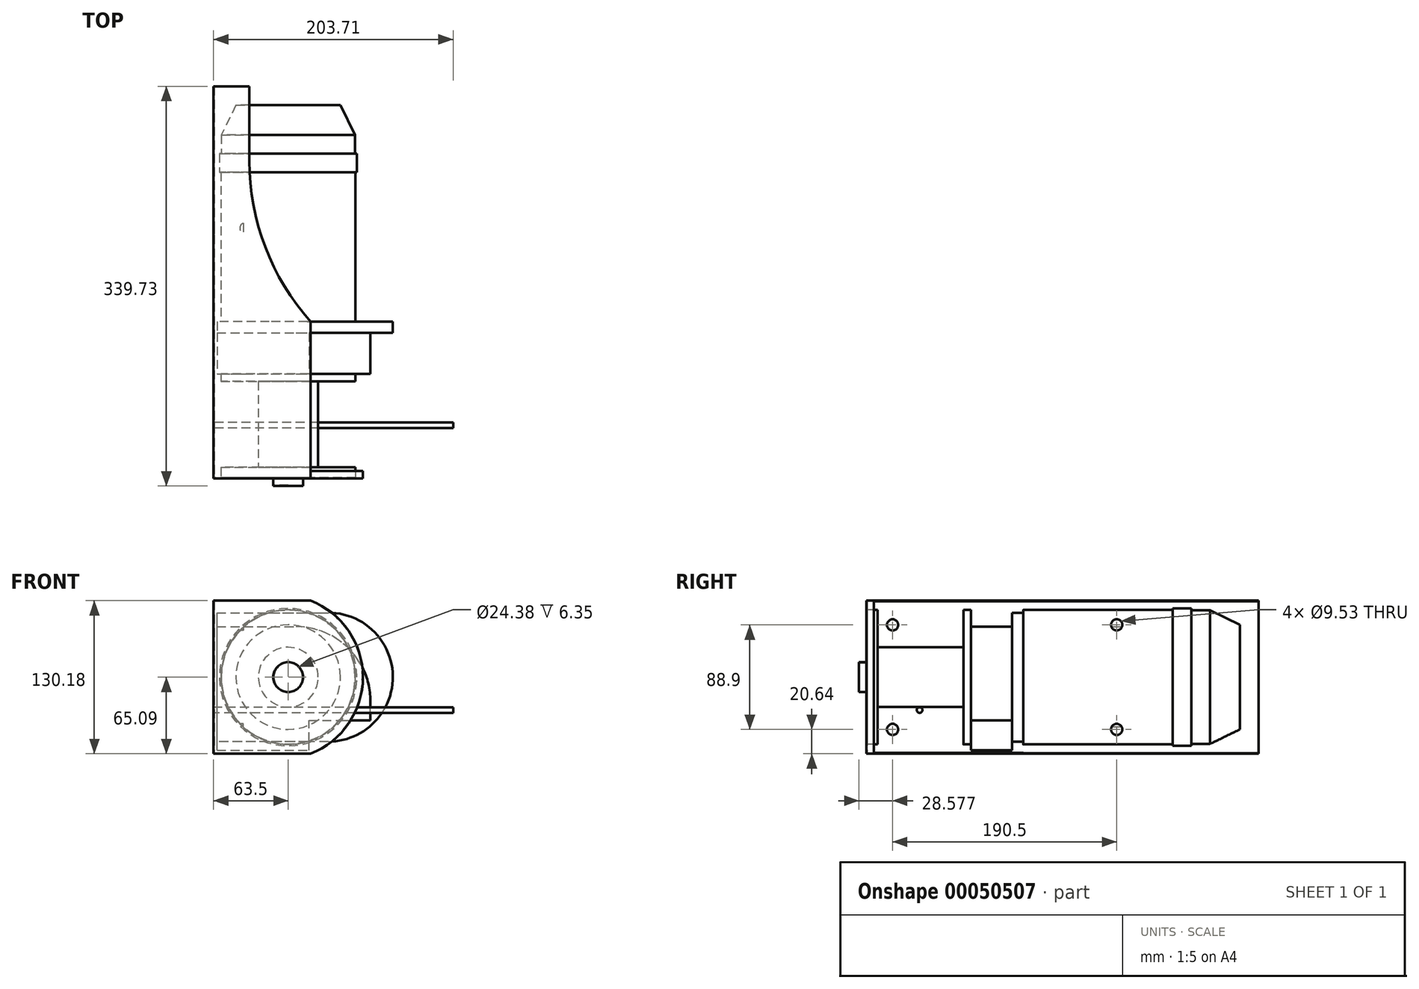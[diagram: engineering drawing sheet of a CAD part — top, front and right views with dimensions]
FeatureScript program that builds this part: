
annotation { "Feature Type Name" : "Feature", "Feature Type Description" : "" }
export const myFeature = defineFeature(function(context is Context, id is Id, definition is map)
    precondition{}
    {
        {
            var Q0;
            Q0=qCreatedBy(makeId("Right.planeOp"),FACE);
            var sketch = newSketch(context, id + "F0", { "sketchPlane" : qUnion([Q0])});
            skLineSegment(sketch, "E0.rect.bottom", {"start": v(166.69, 65.09) * mm, "end": v(-166.69, 65.09) * mm});
            skLineSegment(sketch, "E0.rect.top", {"start": v(166.69, -65.09) * mm, "end": v(-166.69, -65.09) * mm});
            skLineSegment(sketch, "E0.rect.left", {"start": v(166.69, 65.09) * mm, "end": v(166.69, -65.09) * mm});
            skLineSegment(sketch, "E0.rect.right", {"start": v(-166.69, 65.09) * mm, "end": v(-166.69, -65.09) * mm});
            skPoint(sketch, "E0.rect.middle", {"position": v(0, 0) * mm});
            skSolve(sketch);
        }
        {
            var Q0;
            Q0 = qSketchRegion(id + "F0", true);
            extrude(context, id + "F1", {"entities" : qUnion([Q0]), "endBound" : BoundingType.SYMMETRIC, "depth" : 127 * mm});
        }
        {
            var Q0;
            Q0=makeQuery(id+"F1.opExtrude","SWEPT_FACE",FACE,{"disambiguationData":[OSD([sQuery(id+"F0.wireOp",EDGE,"E0.rect.right")])]});
            var sketch = newSketch(context, id + "F2", { "sketchPlane" : qUnion([Q0])});
            skArc(sketch, "E1", {"start": v(19.05, -65.09) * mm, "mid": v(63.5, 0) * mm, "end": v(19.05, 65.09) * mm});
            skLineSegment(sketch, "E2", {"start": v(19.05, 65.09) * mm, "end": v(63.5, 65.09) * mm});
            skLineSegment(sketch, "E3", {"start": v(63.5, 65.09) * mm, "end": v(63.5, -65.09) * mm});
            skLineSegment(sketch, "E4", {"start": v(63.5, -65.09) * mm, "end": v(19.05, -65.09) * mm});
            skSolve(sketch);
        }
        {
            var Q0;
            Q0 = qSketchRegion(id + "F2", true);
            extrude(context, id + "F3", {"entities" : qUnion([Q0]), "operationType" : NewBodyOperationType.REMOVE, "endBound" : BoundingType.UP_TO_NEXT, "oppositeDirection" : true, "depth" : 25.4 * mm});
        }
        {
            var Q0;
            Q0=makeQuery(id+"F1.opExtrude","SWEPT_FACE",FACE,{"disambiguationData":[OSD([sQuery(id+"F0.wireOp",EDGE,"E0.rect.bottom")])]});
            var sketch = newSketch(context, id + "F4", { "sketchPlane" : qUnion([Q0])});
            skLineSegment(sketch, "E5", {"start": v(-33.02, 166.69) * mm, "end": v(-33.02, 103.19) * mm});
            skArc(sketch, "E6", {"start": v(-33.02, 103.19) * mm, "mid": v(-19.56, 30.13) * mm, "end": v(19.05, -33.34) * mm});
            skLineSegment(sketch, "E7", {"start": v(-33.02, 166.69) * mm, "end": v(63.5, 166.69) * mm});
            skLineSegment(sketch, "E8", {"start": v(63.5, 166.69) * mm, "end": v(63.5, -160.34) * mm});
            skLineSegment(sketch, "E9", {"start": v(63.5, -160.34) * mm, "end": v(19.05, -160.34) * mm});
            skLineSegment(sketch, "E10", {"start": v(19.05, -160.34) * mm, "end": v(19.05, -33.34) * mm});
            skSolve(sketch);
        }
        {
            var Q0;
            Q0 = qSketchRegion(id + "F4", true);
            extrude(context, id + "F5", {"entities" : qUnion([Q0]), "operationType" : NewBodyOperationType.REMOVE, "endBound" : BoundingType.UP_TO_NEXT, "oppositeDirection" : true, "depth" : 25.4 * mm});
        }
        {
            var Q0;
            Q0=makeQuery(id+"F1.opExtrude","SWEPT_FACE",FACE,{"disambiguationData":[OSD([sQuery(id+"F0.wireOp",EDGE,"E0.rect.right")])]});
            var sketch = newSketch(context, id + "F6", { "sketchPlane" : qUnion([Q0])});
            skCircle(sketch, "E11", {"center": v(0, 0) * mm, "radius": 12.7 * mm});
            skSolve(sketch);
        }
        {
            var Q0;
            Q0 = qSketchRegion(id + "F6", true);
            extrude(context, id + "F7", {"entities" : qUnion([Q0]), "operationType" : NewBodyOperationType.ADD, "depth" : 6.35 * mm});
        }
        {
            var Q0;
            Q0=makeQuery(id+"F1.opExtrude","SWEPT_FACE",FACE,{"disambiguationData":[OSD([sQuery(id+"F0.wireOp",EDGE,"E0.rect.left")])]});
            var Q1;
            Q1=makeQuery(id+"F5.boolean.opBoolean","COPY",FACE,{"derivedFrom":makeQuery(id+"F5.opExtrude","SWEPT_FACE",FACE,{"disambiguationData":[OSD([sQuery(id+"F4.wireOp",EDGE,"E5")])]})});
            var Q2;
            Q2=makeQuery(id+"F5.boolean.opBoolean","COPY",FACE,{"derivedFrom":makeQuery(id+"F5.opExtrude","SWEPT_FACE",FACE,{"disambiguationData":[OSD([sQuery(id+"F4.wireOp",EDGE,"E6")])]})});
            var Q3;
            Q3=makeQuery(id+"F5.boolean.opBoolean","COPY",FACE,{"derivedFrom":makeQuery(id+"F5.opExtrude","SWEPT_FACE",FACE,{"disambiguationData":[OSD([sQuery(id+"F4.wireOp",EDGE,"E10")])]})});
            var Q4;
            Q4=makeQuery(id+"F5.boolean.opBoolean","COPY",FACE,{"derivedFrom":makeQuery(id+"F5.opExtrude","SWEPT_FACE",FACE,{"disambiguationData":[OSD([sQuery(id+"F4.wireOp",EDGE,"E9")])]})});
            shell(context, id + "F8", {"entities" : qUnion([Q0, Q1, Q2, Q3, Q4]), "thickness" : 0.5 * mm});
        }
        {
            var Q0;
            Q0=makeQuery(id+"F8.opShell","OFFSET_FACE",FACE,{"disambiguationData":[OSD([sQuery(id+"F0.wireOp",EDGE,"E0.rect.right")])]});
            var sketch = newSketch(context, id + "F9", { "sketchPlane" : qUnion([Q0])});
            skCircle(sketch, "E12", {"center": v(0, 0) * mm, "radius": 57.15 * mm});
            skSolve(sketch);
        }
        {
            var Q0;
            Q0 = qSketchRegion(id + "F9", true);
            extrude(context, id + "F10", {"entities" : qUnion([Q0]), "operationType" : NewBodyOperationType.ADD, "depth" : 8.9 * mm});
        }
        {
            var Q0;
            Q0=makeQuery(id+"F10.opExtrude","CAP_FACE",FACE,{"disambiguationData":[OSD([sQuery(id+"F9.wireOp",EDGE,"E12")])],"isStart":false});
            var sketch = newSketch(context, id + "F11", { "sketchPlane" : qUnion([Q0])});
            skCircle(sketch, "E13", {"center": v(0, 0) * mm, "radius": 25.4 * mm});
            skSolve(sketch);
        }
        {
            var Q0;
            Q0 = qSketchRegion(id + "F11", true);
            extrude(context, id + "F12", {"entities" : qUnion([Q0]), "operationType" : NewBodyOperationType.ADD, "depth" : 73.02 * mm});
        }
        {
            var Q0;
            Q0=makeQuery(id+"F12.opExtrude","CAP_FACE",FACE,{"disambiguationData":[OSD([sQuery(id+"F11.wireOp",EDGE,"E13")])],"isStart":false});
            var sketch = newSketch(context, id + "F13", { "sketchPlane" : qUnion([Q0])});
            skCircle(sketch, "E14", {"center": v(0, 0) * mm, "radius": 57.15 * mm});
            skSolve(sketch);
        }
        {
            var Q0;
            Q0 = qSketchRegion(id + "F13", true);
            extrude(context, id + "F14", {"entities" : qUnion([Q0]), "operationType" : NewBodyOperationType.ADD, "depth" : 6.35 * mm});
        }
        {
            var Q0;
            Q0=makeQuery(id+"F14.opExtrude","CAP_FACE",FACE,{"disambiguationData":[OSD([sQuery(id+"F13.wireOp",EDGE,"E14")])],"isStart":false});
            var sketch = newSketch(context, id + "F15", { "sketchPlane" : qUnion([Q0])});
            skLineSegment(sketch, "E15", {"start": v(60.45, -62.04) * mm, "end": v(-17.58, -62.04) * mm});
            skLineSegment(sketch, "E16", {"start": v(-17.58, -62.04) * mm, "end": v(-17.58, -36.64) * mm});
            skLineSegment(sketch, "E17", {"start": v(-17.58, -36.64) * mm, "end": v(-69.85, -36.64) * mm});
            skLineSegment(sketch, "E18", {"start": v(60.45, -62.04) * mm, "end": v(60.45, 42.86) * mm});
            skLineSegment(sketch, "E19", {"start": v(60.45, 42.86) * mm, "end": v(-6.7, 42.86) * mm});
            skLineSegment(sketch, "E20", {"start": v(-69.85, -36.64) * mm, "end": v(-69.85, -20.3) * mm});
            skArc(sketch, "E21", {"start": v(-6.7, 42.86) * mm, "mid": v(-51.35, 24.36) * mm, "end": v(-69.85, -20.3) * mm});
            skSolve(sketch);
        }
        {
            var Q0;
            Q0 = qSketchRegion(id + "F15", true);
            extrude(context, id + "F16", {"entities" : qUnion([Q0]), "operationType" : NewBodyOperationType.ADD, "depth" : 34.92 * mm});
        }
        {
            var Q0;
            Q0=makeQuery(id+"F16.opExtrude","CAP_FACE",FACE,{"disambiguationData":[OSD([sQuery(id+"F15.wireOp",EDGE,"E15"),sQuery(id+"F15.wireOp",EDGE,"E16"),sQuery(id+"F15.wireOp",EDGE,"E17"),sQuery(id+"F15.wireOp",EDGE,"E18"),sQuery(id+"F15.wireOp",EDGE,"E19"),sQuery(id+"F15.wireOp",EDGE,"E20"),sQuery(id+"F15.wireOp",EDGE,"E21")])],"isStart":false});
            var sketch = newSketch(context, id + "F17", { "sketchPlane" : qUnion([Q0])});
            skArc(sketch, "E22", {"start": v(-34.1, 54.8) * mm, "mid": v(-88.9, 0) * mm, "end": v(-34.1, -54.8) * mm});
            skLineSegment(sketch, "E23", {"start": v(-34.1, -54.8) * mm, "end": v(60.45, -54.8) * mm});
            skLineSegment(sketch, "E24", {"start": v(60.45, -54.8) * mm, "end": v(60.45, 54.8) * mm});
            skLineSegment(sketch, "E25", {"start": v(60.45, 54.8) * mm, "end": v(-34.1, 54.8) * mm});
            skLineSegment(sketch, "E26", {"start": v(-34.1, 0) * mm, "end": v(-88.9, 0) * mm, "construction": true});
            skSolve(sketch);
        }
        {
            var Q0;
            Q0 = qSketchRegion(id + "F17", true);
            extrude(context, id + "F18", {"entities" : qUnion([Q0]), "operationType" : NewBodyOperationType.ADD, "depth" : 9.52 * mm});
        }
        {
            var Q0;
            Q0=makeQuery(id+"F18.opExtrude","CAP_FACE",FACE,{"disambiguationData":[OSD([sQuery(id+"F17.wireOp",EDGE,"E22"),sQuery(id+"F17.wireOp",EDGE,"E23"),sQuery(id+"F17.wireOp",EDGE,"E24"),sQuery(id+"F17.wireOp",EDGE,"E25")])],"isStart":false});
            var sketch = newSketch(context, id + "F19", { "sketchPlane" : qUnion([Q0])});
            skCircle(sketch, "E27", {"center": v(0, 0) * mm, "radius": 57.15 * mm});
            skSolve(sketch);
        }
        {
            var Q0;
            Q0 = qSketchRegion(id + "F19", true);
            extrude(context, id + "F20", {"entities" : qUnion([Q0]), "operationType" : NewBodyOperationType.ADD, "depth" : 127 * mm});
        }
        {
            var Q0;
            Q0=qCreatedBy(makeId("Top.planeOp"),FACE);
            var sketch = newSketch(context, id + "F21", { "sketchPlane" : qUnion([Q0])});
            skLineSegment(sketch, "E28", {"start": v(0, 0) * mm, "end": v(0, 93.54) * mm, "construction": true});
            skLineSegment(sketch, "E29", {"start": v(0, 93.54) * mm, "end": v(58.42, 93.54) * mm});
            skLineSegment(sketch, "E30", {"start": v(58.42, 93.54) * mm, "end": v(58.42, 109.41) * mm});
            skLineSegment(sketch, "E31", {"start": v(58.42, 109.41) * mm, "end": v(56.83, 109.41) * mm});
            skLineSegment(sketch, "E32", {"start": v(56.83, 109.41) * mm, "end": v(56.83, 125.29) * mm});
            skLineSegment(sketch, "E33", {"start": v(56.83, 125.29) * mm, "end": v(44.45, 150.69) * mm});
            skLineSegment(sketch, "E34", {"start": v(44.45, 150.69) * mm, "end": v(0, 150.69) * mm});
            skLineSegment(sketch, "E35", {"start": v(0, 93.54) * mm, "end": v(0, 150.69) * mm});
            skSolve(sketch);
        }
        {
            var Q0;
            Q0 = qSketchRegion(id + "F21", true);
            var Q1;
            Q1=sQuery(id+"F21.wireOp",EDGE,"E28");
            revolve(context, id + "F22", {"operationType" : NewBodyOperationType.ADD, "entities" : qUnion([Q0]), "axis" : qUnion([Q1]), "revolveType" : RevolveType.FULL});
        }
        {
            var Q0;
            Q0=makeQuery(id+"F8.opShell","OFFSET_FACE",FACE,{"disambiguationData":[OSD([sQuery(id+"F0.wireOp",EDGE,"E0.rect.bottom"),sQuery(id+"F0.wireOp",EDGE,"E0.rect.top"),sQuery(id+"F0.wireOp",EDGE,"E0.rect.left"),sQuery(id+"F0.wireOp",EDGE,"E0.rect.right")])]});
            var sketch = newSketch(context, id + "F23", { "sketchPlane" : qUnion([Q0])});
            skCircle(sketch, "E36", {"center": v(-121.52, -28) * mm, "radius": 2.38 * mm});
            skSolve(sketch);
        }
        {
            var Q0;
            Q0 = qSketchRegion(id + "F23", true);
            extrude(context, id + "F24", {"entities" : qUnion([Q0]), "operationType" : NewBodyOperationType.ADD, "depth" : 203.2 * mm});
        }
        {
            var Q0;
            Q0=makeQuery(id+"F1.opExtrude","CAP_FACE",FACE,{"disambiguationData":[OSD([sQuery(id+"F0.wireOp",EDGE,"E0.rect.bottom"),sQuery(id+"F0.wireOp",EDGE,"E0.rect.top"),sQuery(id+"F0.wireOp",EDGE,"E0.rect.left"),sQuery(id+"F0.wireOp",EDGE,"E0.rect.right")])],"isStart":true});
            var sketch = newSketch(context, id + "F25", { "sketchPlane" : qUnion([Q0])});
            skCircle(sketch, "E37", {"center": v(-46.04, 44.45) * mm, "radius": 4.76 * mm});
            skCircle(sketch, "E38", {"center": v(144.46, 44.45) * mm, "radius": 4.76 * mm});
            skLineSegment(sketch, "E39.bottom", {"start": v(-46.04, -44.45) * mm, "end": v(144.46, -44.45) * mm, "construction": true});
            skLineSegment(sketch, "E39.top", {"start": v(-46.04, 44.45) * mm, "end": v(144.46, 44.45) * mm, "construction": true});
            skLineSegment(sketch, "E39.left", {"start": v(-46.04, -44.45) * mm, "end": v(-46.04, 44.45) * mm, "construction": true});
            skLineSegment(sketch, "E39.right", {"start": v(144.46, -44.45) * mm, "end": v(144.46, 44.45) * mm, "construction": true});
            skCircle(sketch, "E40", {"center": v(-46.04, -44.45) * mm, "radius": 4.76 * mm});
            skCircle(sketch, "E41", {"center": v(144.46, -44.45) * mm, "radius": 4.76 * mm});
            skSolve(sketch);
        }
        {
            var Q0;
            Q0 = qSketchRegion(id + "F25", true);
            extrude(context, id + "F26", {"entities" : qUnion([Q0]), "operationType" : NewBodyOperationType.REMOVE, "oppositeDirection" : true, "depth" : 25.4 * mm});
        }
    });
